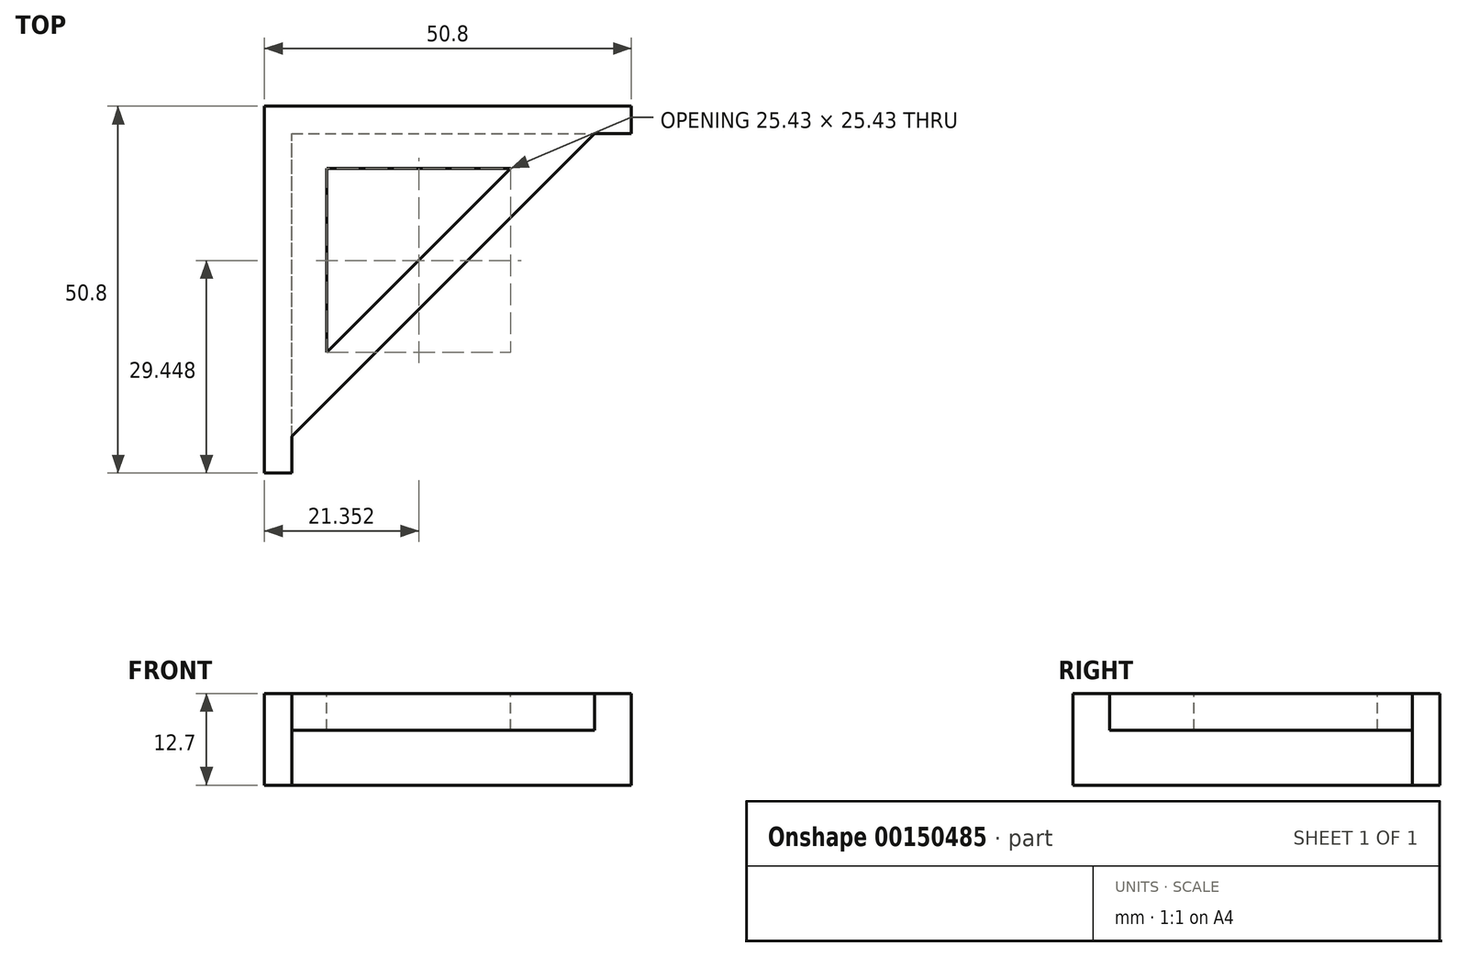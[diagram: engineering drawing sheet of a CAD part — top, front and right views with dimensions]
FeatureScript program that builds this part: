
annotation { "Feature Type Name" : "Feature", "Feature Type Description" : "" }
export const myFeature = defineFeature(function(context is Context, id is Id, definition is map)
    precondition{}
    {
        {
            var Q0;
            Q0=qCreatedBy(makeId("Top.planeOp"),FACE);
            var sketch = newSketch(context, id + "F0", { "sketchPlane" : qUnion([Q0])});
            skLineSegment(sketch, "E0.bottom", {"start": v(0, 0) * mm, "end": v(3.8, 0) * mm});
            skLineSegment(sketch, "E0.top", {"start": v(0, 50.8) * mm, "end": v(3.8, 50.8) * mm});
            skLineSegment(sketch, "E0.left", {"start": v(0, 0) * mm, "end": v(0, 50.8) * mm});
            skLineSegment(sketch, "E0.right", {"start": v(3.81, 0) * mm, "end": v(3.8, 50.8) * mm});
            skLineSegment(sketch, "E1.bottom", {"start": v(3.8, 50.8) * mm, "end": v(50.8, 50.8) * mm});
            skLineSegment(sketch, "E1.top", {"start": v(0.11, 47) * mm, "end": v(50.8, 47) * mm});
            skLineSegment(sketch, "E1.right", {"start": v(50.8, 50.8) * mm, "end": v(50.8, 47) * mm});
            skSolve(sketch);
        }
        {
            var Q0;
            {var subQ1=sQuery(id+"F0.wireOp",EDGE,"E0.bottom");Q0=makeQuery(id+"F0.imprint","IMPRINT",FACE,{"disambiguationData":[TD([[makeQuery(id+"F0.imprint","IMPRINT",EDGE,{"derivedFrom":subQ1}),1.0]])]});}
            var Q1;
            {var subQ0=sQuery(id+"F0.wireOp",EDGE,"E1.bottom");Q1=makeQuery(id+"F0.imprint","IMPRINT",FACE,{"disambiguationData":[TD([[makeQuery(id+"F0.imprint","IMPRINT",EDGE,{"derivedFrom":subQ0}),-1.0]])]});}
            extrude(context, id + "F1", {"entities" : qUnion([Q0, Q1]), "depth" : 12.7 * mm});
        }
        {
            var Q0;
            Q0=makeQuery(id+"F1.opExtrude","CAP_FACE",FACE,{"disambiguationData":[OSD([sQuery(id+"F0.wireOp",EDGE,"E0.bottom"),sQuery(id+"F0.wireOp",EDGE,"E0.top"),sQuery(id+"F0.wireOp",EDGE,"E0.left"),sQuery(id+"F0.wireOp",EDGE,"E0.right"),sQuery(id+"F0.wireOp",EDGE,"E1.bottom"),sQuery(id+"F0.wireOp",EDGE,"E1.top"),sQuery(id+"F0.wireOp",EDGE,"E1.right")])],"isStart":false});
            var sketch = newSketch(context, id + "F2", { "sketchPlane" : qUnion([Q0])});
            skLineSegment(sketch, "E2", {"start": v(3.8, 47) * mm, "end": v(3.8, 5.08) * mm});
            skLineSegment(sketch, "E3", {"start": v(3.8, 5.08) * mm, "end": v(45.72, 47) * mm});
            skLineSegment(sketch, "E4", {"start": v(45.72, 47) * mm, "end": v(3.8, 47) * mm});
            skLineSegment(sketch, "E5.0", {"start": v(34.07, 42.16) * mm, "end": v(8.64, 42.16) * mm});
            skLineSegment(sketch, "E5.1", {"start": v(8.64, 16.73) * mm, "end": v(34.07, 42.16) * mm});
            skLineSegment(sketch, "E5.2", {"start": v(8.64, 42.16) * mm, "end": v(8.64, 16.73) * mm});
            skSolve(sketch);
        }
        {
            var Q0;
            Q0=makeQuery(id+"F2.imprint","IMPRINT",FACE,{"disambiguationData":[TD([[makeQuery(id+"F2.imprint","IMPRINT",EDGE,{"derivedFrom":sQuery(id+"F2.wireOp",EDGE,"E2")}),-1.0]])]});
            extrude(context, id + "F3", {"entities" : qUnion([Q0]), "operationType" : NewBodyOperationType.ADD, "oppositeDirection" : true, "depth" : 5.08 * mm});
        }
    });
